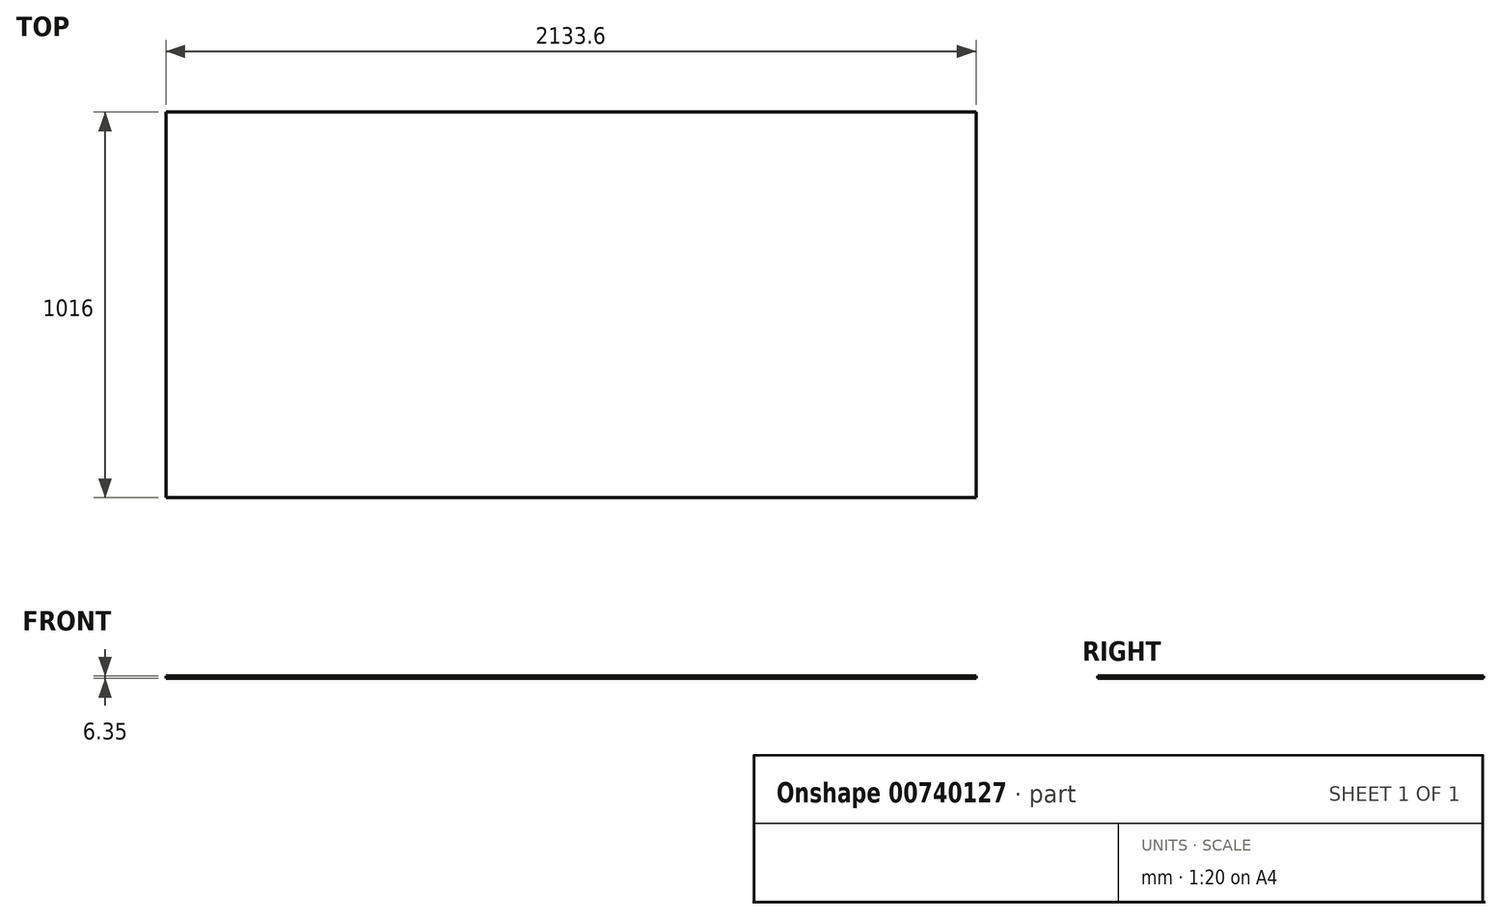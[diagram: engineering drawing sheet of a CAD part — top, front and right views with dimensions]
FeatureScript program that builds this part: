
annotation { "Feature Type Name" : "Feature", "Feature Type Description" : "" }
export const myFeature = defineFeature(function(context is Context, id is Id, definition is map)
    precondition{}
    {
        {
            var Q0;
            Q0=qCreatedBy(makeId("Top.planeOp"),FACE);
            var sketch = newSketch(context, id + "F0", { "sketchPlane" : qUnion([Q0])});
            skLineSegment(sketch, "E0.bottom", {"start": v(2155.9, -203.66) * mm, "end": v(22.3, -203.66) * mm});
            skLineSegment(sketch, "E0.top", {"start": v(2155.9, 812.34) * mm, "end": v(22.3, 812.34) * mm});
            skLineSegment(sketch, "E0.left", {"start": v(2155.9, -203.66) * mm, "end": v(2155.9, 812.34) * mm});
            skLineSegment(sketch, "E0.right", {"start": v(22.3, -203.66) * mm, "end": v(22.3, 812.34) * mm});
            skSolve(sketch);
        }
        {
            var Q0;
            Q0=makeQuery(id+"F0.imprint","IMPRINT",FACE,{"disambiguationData":[TD([[makeQuery(id+"F0.imprint","IMPRINT",EDGE,{"derivedFrom":sQuery(id+"F0.wireOp",EDGE,"E0.right")}),1.0]])]});
            var Q1;
            Q1=makeQuery(id+"F0.imprint","IMPRINT",FACE,{"disambiguationData":[TD([[makeQuery(id+"F0.imprint","IMPRINT",EDGE,{"derivedFrom":sQuery(id+"F0.wireOp",EDGE,"E0.bottom")}),-1.0]])]});
            extrude(context, id + "F1", {"entities" : qUnion([Q0, Q1]), "depth" : 6.35 * mm, "offsetDistance" : 25.4 * mm});
        }
    });
